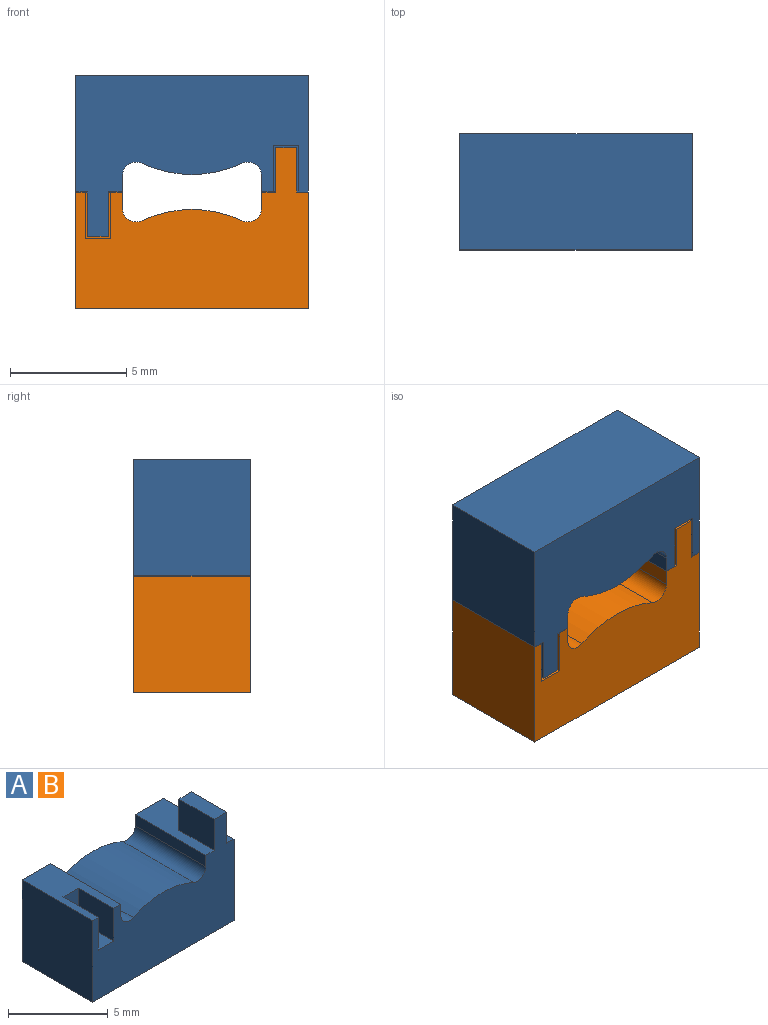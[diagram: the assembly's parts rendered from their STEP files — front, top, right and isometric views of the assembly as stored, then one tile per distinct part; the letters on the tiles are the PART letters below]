
ASSEMBLY  parts=2 mates=1
PART A: 20 faces, bbox 10x5x6.9 mm
  f0: plane 5x2mm, normal (0,0,1), area 7.8mm2, adj f1,f2,f8,f9,f16,f17,f18
  f1: plane 10x6.9mm, normal (0,-1,0), area 43.6mm2, adj f0,f2,f3,f4,f5,f6,f7,f8
  f2: plane 5x0.69mm, normal (-1,0,0), area 3.5mm2, adj f0,f1,f9,f11
  f3: cylinder r=5mm len=5mm, axis (0,1,0), area 22.1mm2, adj f1,f9,f10,f11
  f4: plane 5x0.69mm, normal (1,0,0), area 3.5mm2, adj f1,f5,f9,f10
  f5: plane 5x2mm, normal (0,0,1), area 7.3mm2, adj f1,f4,f6,f9,f12,f13,f14
  f6: plane 5x5mm, normal (-1,0,0), area 25mm2, adj f1,f5,f7,f9
  f7: plane 10x5mm, normal (0,0,-1), area 50mm2, adj f1,f6,f8,f9
  f8: plane 5x5mm, normal (1,0,0), area 25mm2, adj f0,f1,f7,f9
  f9: plane 10x5mm, normal (0,1,0), area 44.1mm2, adj f0,f2,f3,f4,f5,f6,f7,f8
  f10: cylinder r=0.6mm len=5mm, axis (0,1,0), area 6mm2, adj f1,f3,f4,f9
  f11: cylinder r=0.6mm len=5mm, axis (0,1,0), area 6mm2, adj f1,f2,f3,f9
  f12: plane 2x1.1mm, normal (0,-1,0), area 2.2mm2, adj f5,f13,f14,f15
  f13: plane 2.5x2mm, normal (1,0,0), area 5mm2, adj f1,f5,f12,f15
  f14: plane 2.5x2mm, normal (-1,0,0), area 5mm2, adj f1,f5,f12,f15
  f15: plane 2.5x1.1mm, normal (0,0,1), area 2.7mm2, adj f1,f12,f13,f14
  f16: plane 1.9x0.9mm, normal (0,1,0), area 1.7mm2, adj f0,f17,f18,f19
  f17: plane 2.5x1.9mm, normal (-1,0,0), area 4.7mm2, adj f0,f1,f16,f19
  f18: plane 2.5x1.9mm, normal (1,0,0), area 4.7mm2, adj f0,f1,f16,f19
  f19: plane 2.5x0.9mm, normal (0,0,1), area 2.2mm2, adj f1,f16,f17,f18
PART B: same geometry as A
PLACE A rot(axis=(0,-1,0),180deg) t=(7.57,8.17,6.93)mm
PLACE B t=(-2.43,8.17,-3.07)mm fixed
MATE slider B.f5 <-> A.f0  axis (0,0,1) through (-2.43,3.17,1.93)mm
